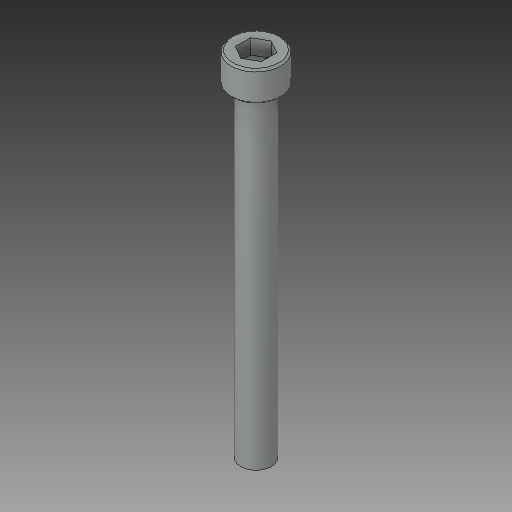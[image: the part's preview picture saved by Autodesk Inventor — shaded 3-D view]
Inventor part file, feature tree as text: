
AUTODESK INVENTOR PART (.ipt)
format: ipt  version: 2017 (Build 210142000, 142)  size: 94,208 bytes
history: native  units: in
note: dims shown in document units (in); Inventor stores cm internally (conversion verified against a paired STEP export)
features: chamfer x1
ambient origin geometry x8: Origin, YZ Plane, XZ Plane, XY Plane, X Axis, Y Axis, Z Axis, Center Point
bodies: Solid1 (feature_tree)
feature tree (1):
  chamfer  "Chamfer2"  [1 undecoded]
note: 1 required parameter value undecoded (feature->parameter linkage not recoverable at this tier; creation-order binding heuristic only, values carry confidence <= 0.55)
